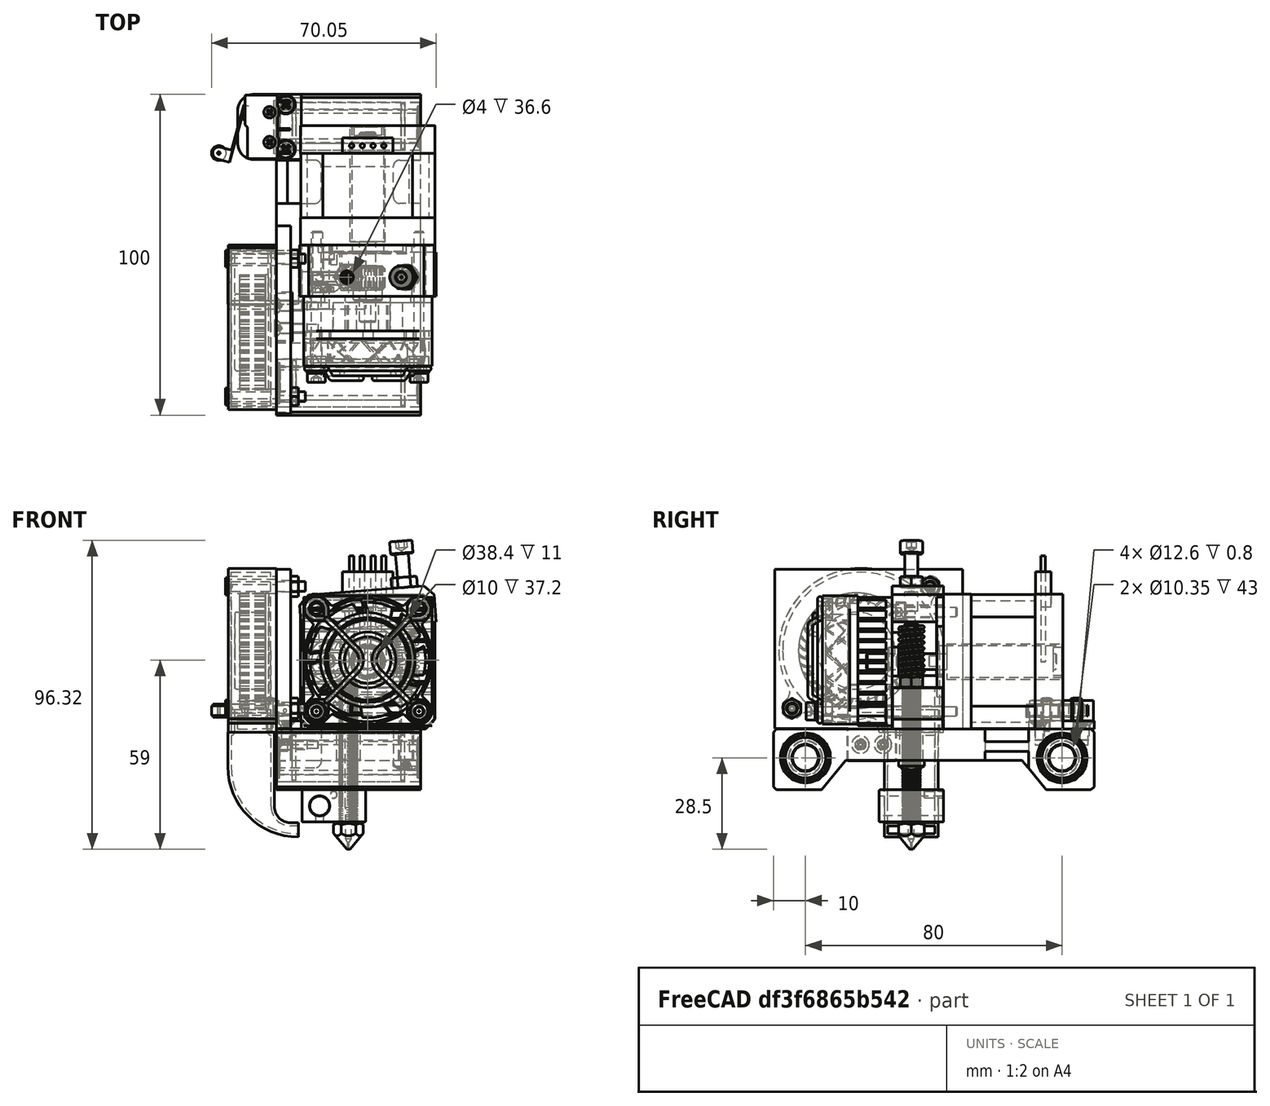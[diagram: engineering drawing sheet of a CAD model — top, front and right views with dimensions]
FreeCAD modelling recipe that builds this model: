
FCSTD DOCUMENT  (FreeCAD 0.18R16117 (Git))
Label: printhead_assembled
License: CreativeCommons Attribution-ShareAlike
LicenseURL: http://creativecommons.org/licenses/by-sa/4.0/
objects: Part::Feature×18, Part::FeaturePython×12, App::DocumentObjectGroup×4, App::Part×1
note: 30 computed .brp shape members not serialized (recipe doc carries the construction recipe); baked Part::Feature solids carry a one-line shape summary decoded from their .brp

FEATURE [Part::Feature] Body001  label="AluSled"
  shape: bbox 45 x 100 x 19 mm, 54 faces (baked)
FEATURE [Part::Feature] Compound001  label="LM8LUU_001"
  Placement = pos=(0,-40,0) rot=(0,1,0;1.5708rad)
  shape: bbox 45 x 15 x 15 mm, 36 faces, 2 solids (baked)
FEATURE [Part::Feature] Compound002  label="LM8LUU_002"
  Placement = pos=(0,40,0) rot=(0,1,0;1.5708rad)
  shape: bbox 45 x 15 x 15 mm, 36 faces, 2 solids (baked)
FEATURE [Part::Feature] Compound004  label="Nema17_38mm_001"
  Placement = pos=(6,3,30) rot=(0.57735,-0.57735,0.57735;2.0944rad)
  shape: bbox 42 x 61.2 x 54 mm, 83 faces, 8 solids (baked)
FEATURE [Part::Feature] Compound005  label="Extruder_MK8"
  Placement = pos=(6,3,30) rot=(0,0,1;0rad)
  shape: bbox 42.54 x 21.7 x 71.64 mm, 366 faces, 7 solids (baked)
FEATURE [App::DocumentObjectGroup] Group001  label="extruder"
  Group = -> [Compound004,Compound005]
FEATURE [Part::Feature] Compound006  label="TeflonThroatTube_40mm"
  Placement = pos=(0,-7,-15.5) rot=(0,0,1;0rad)
  shape: bbox 6 x 6 x 40 mm, 146 faces, 2 solids (baked)
FEATURE [Part::Feature] Body002  label="Nozzle_0.4mm"
  Placement = pos=(0,-7,-15.5) rot=(0,0,1;0rad)
  shape: bbox 9.238 x 9.238 x 13 mm, 33 faces (baked)
FEATURE [Part::Feature] Body003  label="AluHeaterBlock"
  Placement = pos=(0,-7,-20) rot=(0,0,1;0rad)
  shape: bbox 19.8 x 20 x 10 mm, 37 faces (baked)
FEATURE [Part::Feature] Body004  label="HeatSink"
  Placement = pos=(6,-13,30) rot=(0,0,1;0rad)
  shape: bbox 40 x 10.7 x 40 mm, 117 faces (baked)
FEATURE [Part::Feature] Compound007  label="4010_DC-Fan_001"
  Placement = pos=(6,-23.7,30.5) rot=(0,0,1;0rad)
  shape: bbox 40 x 18 x 40 mm, 120 faces, 2 solids (baked)
FEATURE [Part::Feature] Compound008  label="micro switch 5A 125V 250V ~ 10T85u_001"
  Placement = pos=(-24.6,39.85,14.7) rot=(0,0,1;0rad)
  shape: bbox 24.69 x 20.93 x 6.4 mm, 78 faces, 4 solids (baked)
FEATURE [Part::Feature] Body005  label="EndSwitch_X-Holder"
  Placement = pos=(-19.5,39.85,9) rot=(0,0,1;0rad)
  shape: bbox 19.8 x 20.3 x 2.5 mm, 14 faces (baked)
FEATURE [Part::Feature] Compound009  label="FanGrill"
  Placement = pos=(6,-35.5,30.5) rot=(0,0,1;3.14159rad)
  shape: bbox 40.12 x 4.644 x 40.12 mm, 34 faces, 4 solids (baked)
FEATURE [Part::Feature] Body006  label="5015_air-blower_holder"
  Placement = pos=(-22.5,-26.7,9.1) rot=(0,0,1;0rad)
  shape: bbox 4.5 x 58.6 x 59.7 mm, 16 faces (baked)
FEATURE [Part::Feature] Fusion001  label="5015_CentrifugalFan"
  Placement = pos=(-22.5,3,8) rot=(-0.57735,0.57735,0.57735;4.18879rad)
  shape: bbox 15 x 51.3 x 51.05 mm, 225 faces, 2 solids (baked)
FEATURE [Part::Feature] Body007  label="FanDuct"
  Placement = pos=(-37.6,-7,-24.7) rot=(0,0,1;0rad)
  shape: bbox 22 x 16.8 x 39.7 mm, 26 faces (baked)
FEATURE [Part::FeaturePython] Screw  label="M3x6-Screw_001"  # Fasteners workbench fastener (typed FeaturePython)
  Placement = pos=(-19.5,32.9,11.5) rot=(0,0,1;0rad)
  diameter = 4
  invert = false
  length = 2
  matchOuter = false
  offset = 0
  thread = false
  type = 17
FEATURE [Part::FeaturePython] Screw001  label="M3x6-Screw_002"  # Fasteners workbench fastener (typed FeaturePython)
  Placement = pos=(-19.5,46.8,11.5) rot=(0,0,1;0rad)
  diameter = 4
  invert = false
  length = 2
  matchOuter = false
  offset = 0
  thread = false
  type = 17
FEATURE [Part::FeaturePython] Screw002  label="M2x10-Screw_001"  # Fasteners workbench fastener (typed FeaturePython)
  Placement = pos=(-24.6,35.1,18.3) rot=(0,0,1;0rad)
  diameter = 2
  invert = false
  length = 5
  matchOuter = false
  offset = 0
  thread = false
  type = 18
FEATURE [Part::FeaturePython] Screw003  label="M2x10-Screw"  # Fasteners workbench fastener (typed FeaturePython)
  Placement = pos=(-24.6,44.4,18.3) rot=(0,0,1;0rad)
  diameter = 2
  invert = false
  length = 5
  matchOuter = false
  offset = 0
  thread = false
  type = 18
FEATURE [App::DocumentObjectGroup] Group  label="carrier"
  Group = -> [Body001,Compound001,Compound002,Body005,Compound008,Screw,Screw001,Screw002,Screw003]
FEATURE [Part::FeaturePython] Washer  label="M3-Washer_001"  # Fasteners workbench fastener (typed FeaturePython)
  Placement = pos=(22,-36.8,14.5) rot=(1,0,0;4.71239rad)
  diameter = 4
  invert = false
  matchOuter = false
  offset = 0
  type = 2
FEATURE [Part::FeaturePython] Washer001  label="M3-Washer_002"  # Fasteners workbench fastener (typed FeaturePython)
  Placement = pos=(-10,-36.8,14.5) rot=(1,0,0;4.71239rad)
  diameter = 4
  invert = false
  matchOuter = false
  offset = 0
  type = 2
FEATURE [Part::Feature] Body008  label="M3x44-Screw_001"
  Placement = pos=(-10,-36.8,14.5) rot=(1,0,0;1.5708rad)
  shape: bbox 5.953 x 47 x 5.953 mm, 31 faces (baked)
FEATURE [Part::Feature] Body009  label="M3x44-Screw_002"
  Placement = pos=(22,-36.8,14.5) rot=(1,0,0;1.5708rad)
  shape: bbox 5.953 x 47 x 5.953 mm, 31 faces (baked)
FEATURE [App::DocumentObjectGroup] Group002  label="hotend"
  Group = -> [Compound006,Body002,Body003,Body004,Compound007,Compound009,Washer,Washer001,Body008,Body009]
FEATURE [Part::FeaturePython] Screw004  label="M3x25-Screw_001"  # Fasteners workbench fastener (typed FeaturePython)
  Placement = pos=(-38.4,-1.2,53.4) rot=(0,1,0;4.71239rad)
  diameter = 4
  invert = false
  length = 9
  matchOuter = false
  offset = 0
  thread = false
  type = 17
FEATURE [Part::FeaturePython] Screw005  label="M3x25-Screw_002"  # Fasteners workbench fastener (typed FeaturePython)
  Placement = pos=(-38.4,-44.2,15.4) rot=(0,-1,0;1.5708rad)
  diameter = 4
  invert = false
  length = 9
  matchOuter = false
  offset = 0
  thread = false
  type = 17
FEATURE [Part::FeaturePython] Nut  label="M3-Nut_001"  # Fasteners workbench fastener (typed FeaturePython)
  Placement = pos=(-18,-44.2,15.4) rot=(0,1,0;1.5708rad)
  diameter = 4
  invert = false
  matchOuter = false
  offset = 0
  thread = false
  type = 4
FEATURE [Part::FeaturePython] Nut001  label="M3-Nut_002"  # Fasteners workbench fastener (typed FeaturePython)
  Placement = pos=(-18,-1.2,53.4) rot=(0,1,0;1.5708rad)
  diameter = 4
  invert = false
  matchOuter = false
  offset = 0
  thread = false
  type = 4
FEATURE [Part::FeaturePython] Screw006  label="M3x10-Screw_001"  # Fasteners workbench fastener (typed FeaturePython)
  Placement = pos=(-23,-22.85,4.1) rot=(0,1,0;4.71239rad)
  diameter = 4
  invert = false
  length = 4
  matchOuter = false
  offset = 0
  thread = false
  type = 17
FEATURE [Part::FeaturePython] Screw007  label="M3x10-Screw_002"  # Fasteners workbench fastener (typed FeaturePython)
  Placement = pos=(-23,-15.85,4.1) rot=(0,1,0;4.71239rad)
  diameter = 4
  invert = false
  length = 4
  matchOuter = false
  offset = 0
  thread = false
  type = 17
FEATURE [App::DocumentObjectGroup] Group003  label="part-cooling"
  Group = -> [Body006,Fusion001,Body007,Screw004,Screw005,Nut,Nut001,Screw006,Screw007]
FEATURE [App::Part] Part  label="A3/A6_Printhead"
  Group = -> [Body005,Compound002,Compound001,Body001,Compound008,Screw,Screw002,Screw001,Screw003,Group,Compound004,Compound005,Group001,Body008,Compound006,Body002,Body003,Body004,Compound007,Compound009,Body009,Washer001,Washer,Group002,Screw004,Screw006,Screw007,Nut,Screw005,Nut001,Fusion001,Body006,Body007,Group003]
  Origin = -> Origin
